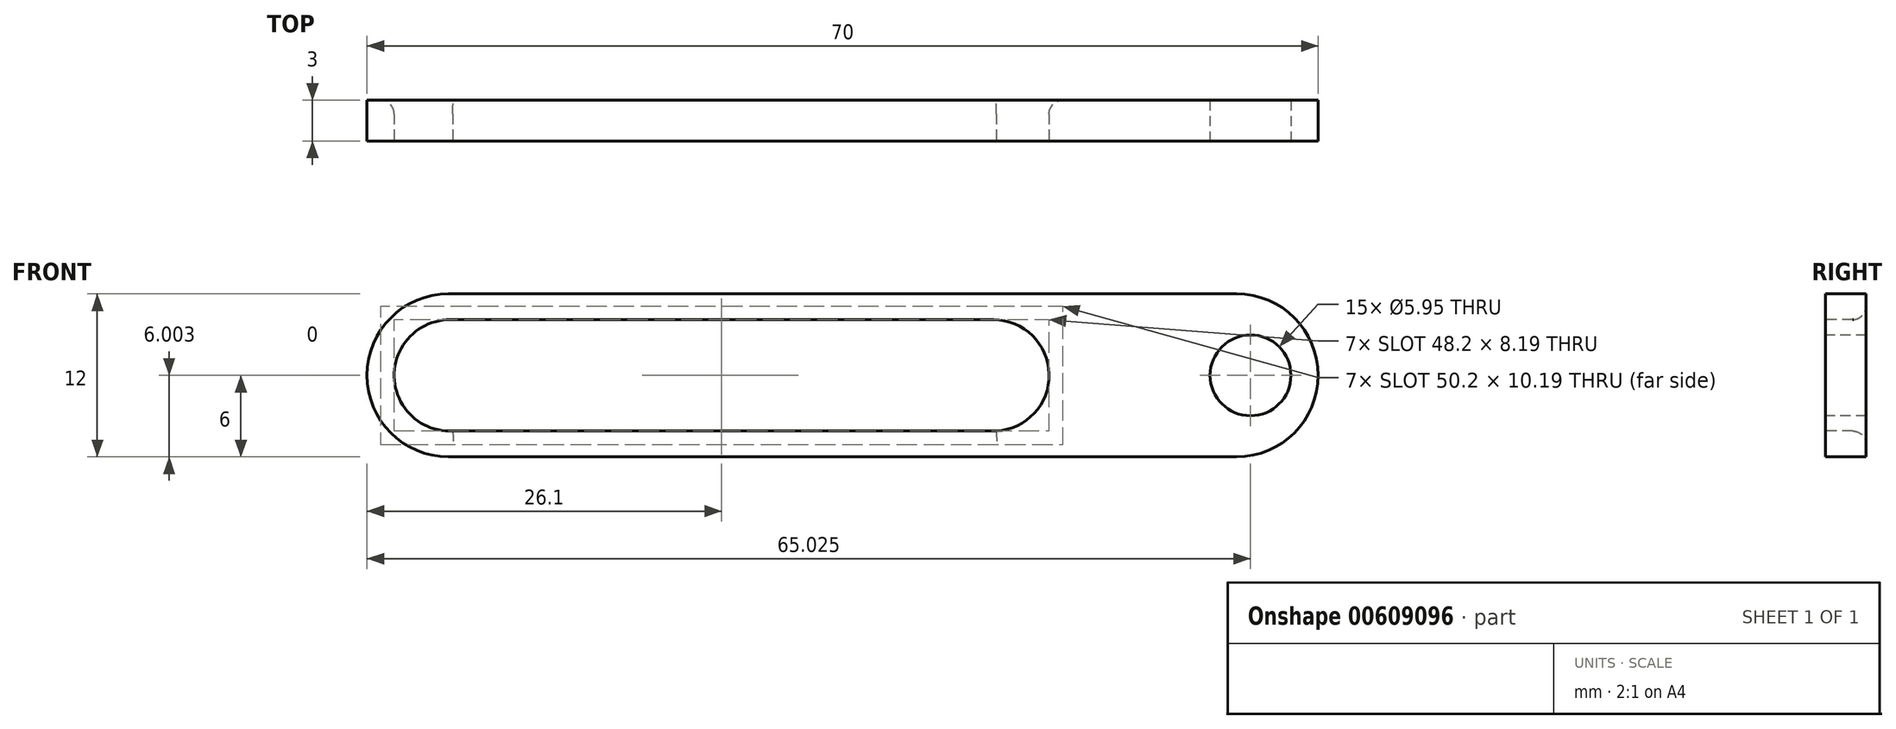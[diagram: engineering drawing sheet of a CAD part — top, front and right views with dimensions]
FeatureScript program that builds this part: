
annotation { "Feature Type Name" : "Feature", "Feature Type Description" : "" }
export const myFeature = defineFeature(function(context is Context, id is Id, definition is map)
    precondition{}
    {
        {
            var Q0;
            Q0=qCreatedBy(makeId("Front.planeOp"),FACE);
            var sketch = newSketch(context, id + "F0", { "sketchPlane" : qUnion([Q0])});
            skLineSegment(sketch, "E0.bottom", {"start": v(-35, 6) * mm, "end": v(35, 6) * mm});
            skLineSegment(sketch, "E0.top", {"start": v(-35, -6) * mm, "end": v(35, -6) * mm});
            skLineSegment(sketch, "E0.left", {"start": v(-35, 6) * mm, "end": v(-35, -6) * mm});
            skLineSegment(sketch, "E0.right", {"start": v(35, 6) * mm, "end": v(35, -6) * mm});
            skPoint(sketch, "E0.middle", {"position": v(0, 0) * mm});
            skSolve(sketch);
        }
        {
            var Q0;
            Q0=makeQuery(id+"F0.imprint","IMPRINT",FACE,{"disambiguationData":[TD([[makeQuery(id+"F0.imprint","IMPRINT",EDGE,{"derivedFrom":sQuery(id+"F0.wireOp",EDGE,"E0.bottom")}),-1.0]])]});
            extrude(context, id + "F1", {"entities" : qUnion([Q0]), "depth" : 3 * mm, "offsetDistance" : 25 * mm});
        }
        {
            var Q0;
            Q0=makeQuery(id+"F1.opExtrude","SWEPT_EDGE",EDGE,{"disambiguationData":[OSD([sQuery(id+"F0.wireOp",EDGE,"E0.bottom"),sQuery(id+"F0.wireOp",EDGE,"E0.left")])]});
            var Q1;
            Q1=makeQuery(id+"F1.opExtrude","SWEPT_EDGE",EDGE,{"disambiguationData":[OSD([sQuery(id+"F0.wireOp",EDGE,"E0.top"),sQuery(id+"F0.wireOp",EDGE,"E0.left")])]});
            var Q2;
            Q2=makeQuery(id+"F1.opExtrude","SWEPT_EDGE",EDGE,{"disambiguationData":[OSD([sQuery(id+"F0.wireOp",EDGE,"E0.bottom"),sQuery(id+"F0.wireOp",EDGE,"E0.right")])]});
            var Q3;
            Q3=makeQuery(id+"F1.opExtrude","SWEPT_EDGE",EDGE,{"disambiguationData":[OSD([sQuery(id+"F0.wireOp",EDGE,"E0.top"),sQuery(id+"F0.wireOp",EDGE,"E0.right")])]});
            fillet(context, id + "F2", {"entities" : qUnion([Q0, Q1, Q2, Q3]), "radius" : 6 * mm, "tangentPropagation" : true, "allowEdgeOverflow" : false});
        }
        {
            var Q0;
            Q0=makeQuery(id+"F1.opExtrude","CAP_FACE",FACE,{"disambiguationData":[OSD([sQuery(id+"F0.wireOp",EDGE,"E0.bottom"),sQuery(id+"F0.wireOp",EDGE,"E0.top"),sQuery(id+"F0.wireOp",EDGE,"E0.left"),sQuery(id+"F0.wireOp",EDGE,"E0.right")])],"isStart":false});
            var sketch = newSketch(context, id + "F3", { "sketchPlane" : qUnion([Q0])});
            skCircle(sketch, "E1", {"center": v(-28.9, 0) * mm, "radius": 4.1 * mm});
            skCircle(sketch, "E2", {"center": v(30.03, 0) * mm, "radius": 2.98 * mm});
            skCircle(sketch, "E3", {"center": v(11.1, 0) * mm, "radius": 4.1 * mm});
            skLineSegment(sketch, "E4.bottom", {"start": v(-28.88, 4.1) * mm, "end": v(11.32, 4.1) * mm});
            skLineSegment(sketch, "E4.top", {"start": v(-28.88, -4.1) * mm, "end": v(11.32, -4.1) * mm});
            skLineSegment(sketch, "E4.left", {"start": v(-28.88, 4.1) * mm, "end": v(-28.88, -4.1) * mm});
            skLineSegment(sketch, "E4.right", {"start": v(11.32, 4.1) * mm, "end": v(11.32, -4.1) * mm});
            skSolve(sketch);
        }
        {
            var Q0;
            {var subQ0=sQuery(id+"F3.wireOp",EDGE,"E4.left");Q0=makeQuery(id+"F3.imprint","IMPRINT",FACE,{"disambiguationData":[TD([[makeQuery(id+"F3.imprint","IMPRINT",EDGE,{"derivedFrom":subQ0}),-1.0]])]});}
            var Q1;
            {var subQ0=sQuery(id+"F3.wireOp",EDGE,"E4.left");Q1=makeQuery(id+"F3.imprint","IMPRINT",FACE,{"disambiguationData":[TD([[makeQuery(id+"F3.imprint","IMPRINT",EDGE,{"derivedFrom":subQ0}),1.0]])]});}
            var Q2;
            {var subQ0=sQuery(id+"F3.wireOp",EDGE,"E4.bottom");var subQ5=sQuery(id+"F3.wireOp",EDGE,"E3");var subQ6=makeQuery(id+"F3.imprint","INTERSECT",VERTEX,{"disambiguationData":[OD(1.0)],"derivedFrom":[subQ5,subQ0]});Q2=makeQuery(id+"F3.imprint","IMPRINT",FACE,{"disambiguationData":[TD([[makeQuery(id+"F3.imprint","IMPRINT",EDGE,{"disambiguationData":[TD([[subQ6,-1.0]])],"derivedFrom":subQ5}),-1.0]])]});}
            var Q3;
            {var subQ0=sQuery(id+"F3.wireOp",EDGE,"E4.bottom");var subQ1=sQuery(id+"F3.wireOp",EDGE,"E3");var subQ2=makeQuery(id+"F3.imprint","INTERSECT",VERTEX,{"disambiguationData":[OD(0.0)],"derivedFrom":[subQ1,subQ0]});Q3=makeQuery(id+"F3.imprint","IMPRINT",FACE,{"disambiguationData":[TD([[makeQuery(id+"F3.imprint","IMPRINT",EDGE,{"disambiguationData":[TD([[subQ2,1.0]])],"derivedFrom":subQ1}),1.0]])]});}
            var Q4;
            {var subQ0=sQuery(id+"F3.wireOp",EDGE,"E4.right");var subQ1=sQuery(id+"F3.wireOp",EDGE,"E3");var subQ3=makeQuery(id+"F3.imprint","INTERSECT",VERTEX,{"derivedFrom":[subQ1,subQ0]});Q4=makeQuery(id+"F3.imprint","IMPRINT",FACE,{"disambiguationData":[TD([[makeQuery(id+"F3.imprint","IMPRINT",EDGE,{"disambiguationData":[TD([[subQ3,1.0]])],"derivedFrom":subQ1}),1.0]])]});}
            var Q5;
            Q5=makeQuery(id+"F3.imprint","IMPRINT",FACE,{"disambiguationData":[TD([[makeQuery(id+"F3.imprint","IMPRINT",EDGE,{"derivedFrom":sQuery(id+"F3.wireOp",EDGE,"E2")}),1.0]])]});
            extrude(context, id + "F4", {"entities" : qUnion([Q0, Q1, Q2, Q3, Q4, Q5]), "operationType" : NewBodyOperationType.REMOVE, "oppositeDirection" : true, "depth" : 5 * mm, "offsetDistance" : 25 * mm});
        }
        {
            var Q0;
            Q0=makeQuery(id+"F4.boolean.opBoolean","INTERSECT",EDGE,{"derivedFrom":[makeQuery(id+"F1.opExtrude","CAP_FACE",FACE,{"disambiguationData":[OSD([sQuery(id+"F0.wireOp",EDGE,"E0.bottom"),sQuery(id+"F0.wireOp",EDGE,"E0.top"),sQuery(id+"F0.wireOp",EDGE,"E0.left"),sQuery(id+"F0.wireOp",EDGE,"E0.right")])],"isStart":true}),makeQuery(id+"F4.opExtrude","SWEPT_FACE",FACE,{"disambiguationData":[OSD([sQuery(id+"F3.wireOp",EDGE,"E4.bottom")])]})]});
            var Q1;
            Q1=makeQuery(id+"F4.boolean.opBoolean","INTERSECT",EDGE,{"derivedFrom":[makeQuery(id+"F1.opExtrude","CAP_FACE",FACE,{"disambiguationData":[OSD([sQuery(id+"F0.wireOp",EDGE,"E0.bottom"),sQuery(id+"F0.wireOp",EDGE,"E0.top"),sQuery(id+"F0.wireOp",EDGE,"E0.left"),sQuery(id+"F0.wireOp",EDGE,"E0.right")])],"isStart":true}),makeQuery(id+"F4.opExtrude","SWEPT_FACE",FACE,{"disambiguationData":[OSD([sQuery(id+"F3.wireOp",EDGE,"E1")])]})]});
            var Q2;
            Q2=makeQuery(id+"F4.boolean.opBoolean","INTERSECT",EDGE,{"derivedFrom":[makeQuery(id+"F1.opExtrude","CAP_FACE",FACE,{"disambiguationData":[OSD([sQuery(id+"F0.wireOp",EDGE,"E0.bottom"),sQuery(id+"F0.wireOp",EDGE,"E0.top"),sQuery(id+"F0.wireOp",EDGE,"E0.left"),sQuery(id+"F0.wireOp",EDGE,"E0.right")])],"isStart":true}),makeQuery(id+"F4.opExtrude","SWEPT_FACE",FACE,{"disambiguationData":[OSD([sQuery(id+"F3.wireOp",EDGE,"E4.top")])]})]});
            var Q3;
            Q3=makeQuery(id+"F4.boolean.opBoolean","COPY",EDGE,{"derivedFrom":makeQuery(id+"F4.opExtrude","CAP_EDGE",EDGE,{"disambiguationData":[OSD([sQuery(id+"F3.wireOp",EDGE,"E4.bottom")])],"isStart":true})});
            var Q4;
            Q4=makeQuery(id+"F4.boolean.opBoolean","COPY",EDGE,{"derivedFrom":makeQuery(id+"F4.opExtrude","CAP_EDGE",EDGE,{"disambiguationData":[OSD([sQuery(id+"F3.wireOp",EDGE,"E1")])],"isStart":true})});
            var Q5;
            Q5=makeQuery(id+"F4.boolean.opBoolean","COPY",EDGE,{"derivedFrom":makeQuery(id+"F4.opExtrude","CAP_EDGE",EDGE,{"disambiguationData":[OSD([sQuery(id+"F3.wireOp",EDGE,"E4.top")])],"isStart":true})});
            var Q6;
            Q6=makeQuery(id+"F4.boolean.opBoolean","COPY",EDGE,{"derivedFrom":makeQuery(id+"F4.opExtrude","CAP_EDGE",EDGE,{"disambiguationData":[OSD([sQuery(id+"F3.wireOp",EDGE,"E3")])],"isStart":true})});
            fillet(context, id + "F5", {"entities" : qUnion([Q0, Q1, Q2, Q3, Q4, Q5, Q6]), "radius" : 1 * mm, "tangentPropagation" : true, "allowEdgeOverflow" : false});
        }
    });
